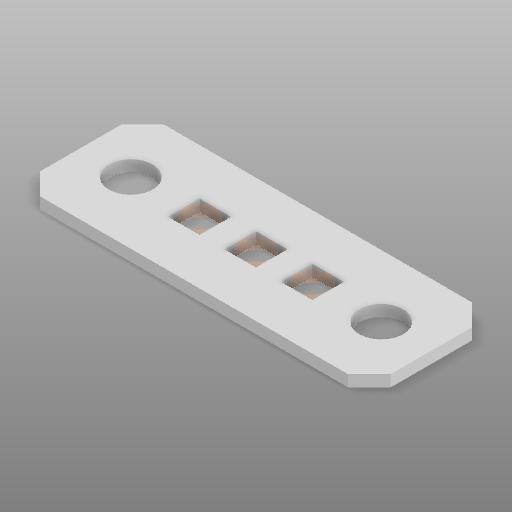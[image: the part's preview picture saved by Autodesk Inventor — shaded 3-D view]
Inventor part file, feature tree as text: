
AUTODESK INVENTOR PART (.ipt)
format: ipt  version: 2021 (Build 250183000, 183)  size: 179,712 bytes
history: native  units: in
note: dims shown in document units (in); Inventor stores cm internally (conversion verified against a paired STEP export)
features: other x4, sketch x3, extrude x3, imported_body x1
ambient origin geometry x8: Origin, YZ Plane, XZ Plane, XY Plane, X Axis, Y Axis, Z Axis, Center Point
bodies: Body1 (feature_tree), Body2 (feature_tree), Body3 (feature_tree), Body4 (feature_tree)
feature tree (11):
  parser-record x1  (decoder bookkeeping rows leaked as tree rows — omitted from the tree; the rows remain in map.json)
  imported_body  "Base1"
  sketch  "Sketch4"  dims[d18=1.0in d19=0.0in d20=1.0in d21=0.0in]
  other  "Srf1"
  sketch  "Sketch5"  dims[d22=1.0in d23=0.0in]
  other  "Srf2"
  sketch  "Sketch6"
  other  "Srf3"
  extrude  "ExtrusionSrf1"  Depth=1.0in TaperAngle=0.0deg
  extrude  "ExtrusionSrf2"  [1 undecoded]
  extrude  "ExtrusionSrf3"  [1 undecoded]
note: 2 required parameter values undecoded (feature->parameter linkage not recoverable at this tier; creation-order binding heuristic only, values carry confidence <= 0.55)
